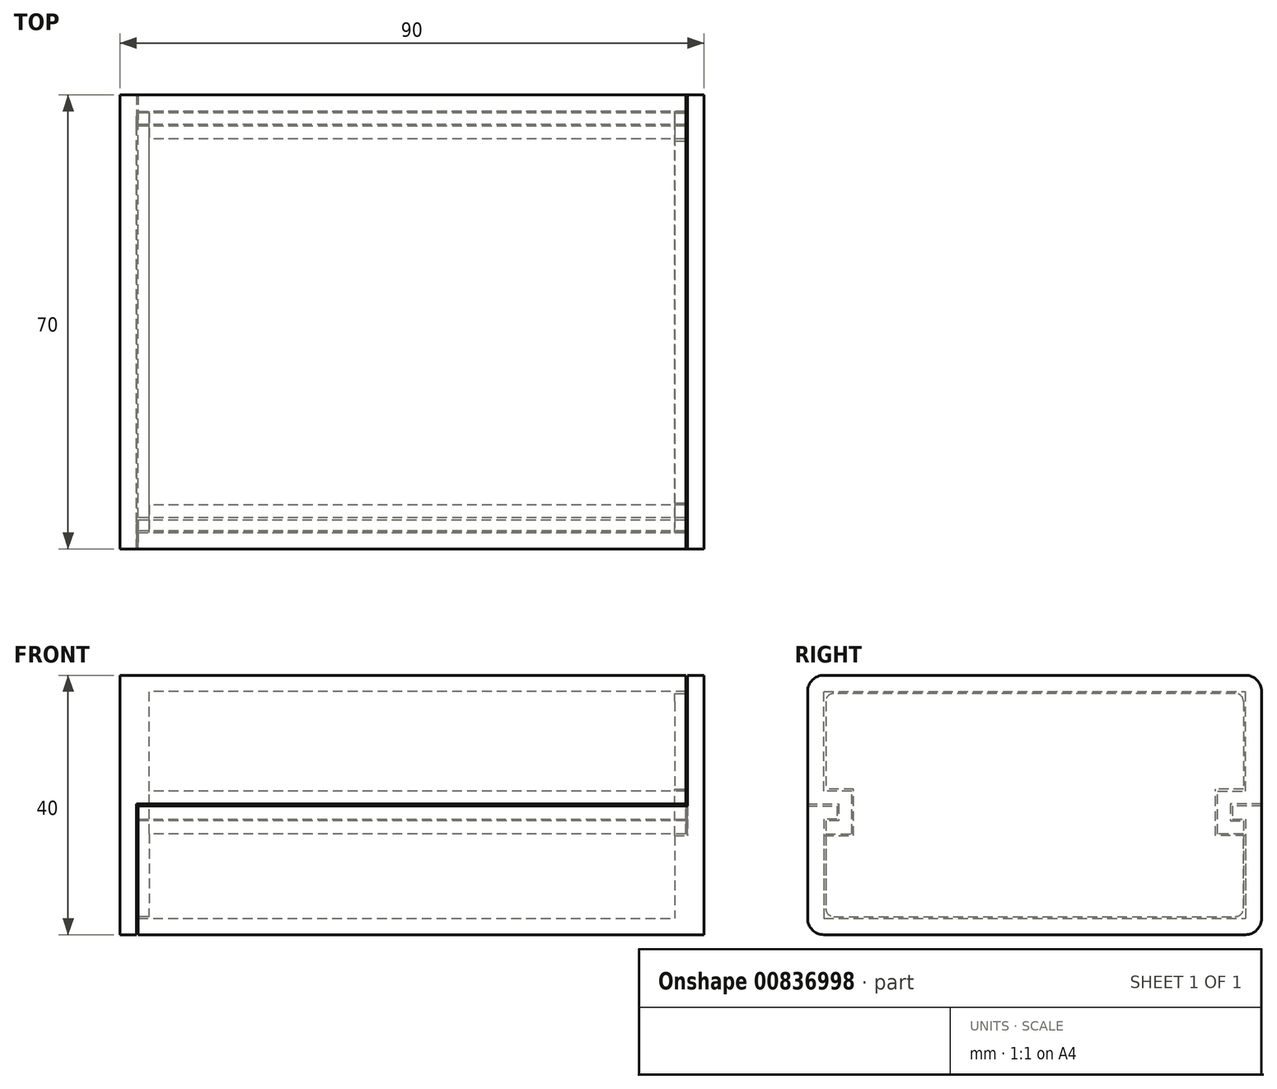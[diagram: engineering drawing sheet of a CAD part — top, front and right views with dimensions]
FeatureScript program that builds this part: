
annotation { "Feature Type Name" : "Feature", "Feature Type Description" : "" }
export const myFeature = defineFeature(function(context is Context, id is Id, definition is map)
    precondition{}
    {
        {
            assignVariable(context, id + "F0", {"name" : "LipSize", "anyValue" : 2});
        }
        {
            assignVariable(context, id + "F1", {"name" : "Thickness", "anyValue" : 2.5});
        }
        {
            var Q0;
            Q0=qCreatedBy(makeId("Top.planeOp"),FACE);
            var sketch = newSketch(context, id + "F2", { "sketchPlane" : qUnion([Q0])});
            skLineSegment(sketch, "E0.bottom", {"start": v(-45, 35) * mm, "end": v(45, 35) * mm});
            skLineSegment(sketch, "E0.top", {"start": v(-45, -35) * mm, "end": v(45, -35) * mm});
            skLineSegment(sketch, "E0.left", {"start": v(-45, 35) * mm, "end": v(-45, -35) * mm});
            skLineSegment(sketch, "E0.right", {"start": v(45, 35) * mm, "end": v(45, -35) * mm});
            skLineSegment(sketch, "E1", {"start": v(-42.5, 35) * mm, "end": v(-42.5, -35) * mm, "construction": true});
            skLineSegment(sketch, "E2", {"start": v(42.5, 35) * mm, "end": v(42.5, -35) * mm, "construction": true});
            skLineSegment(sketch, "E3", {"start": v(42.2, 35) * mm, "end": v(42.2, -35) * mm, "construction": true});
            skLineSegment(sketch, "E4", {"start": v(-42.2, 35) * mm, "end": v(-42.2, -35) * mm, "construction": true});
            skSolve(sketch);
        }
        {
            var Q0;
            Q0=qCreatedBy(makeId("Right.planeOp"),FACE);
            var sketch = newSketch(context, id + "F3", { "sketchPlane" : qUnion([Q0])});
            skLineSegment(sketch, "E5.bottom", {"start": v(-35, 20) * mm, "end": v(35, 20) * mm});
            skLineSegment(sketch, "E5.top", {"start": v(-35, -20) * mm, "end": v(35, -20) * mm});
            skLineSegment(sketch, "E5.left", {"start": v(-35, 20) * mm, "end": v(-35, -20) * mm});
            skLineSegment(sketch, "E5.right", {"start": v(35, 20) * mm, "end": v(35, -20) * mm});
            skLineSegment(sketch, "E6", {"start": v(-35, 0) * mm, "end": v(35, 0) * mm, "construction": true});
            skLineSegment(sketch, "E7", {"start": v(35, 17.5) * mm, "end": v(-35, 17.5) * mm, "construction": true});
            skLineSegment(sketch, "E8", {"start": v(35, 17.2) * mm, "end": v(-35, 17.2) * mm, "construction": true});
            skLineSegment(sketch, "E9", {"start": v(35, -17.5) * mm, "end": v(-35, -17.5) * mm, "construction": true});
            skLineSegment(sketch, "E10", {"start": v(-35, -17.2) * mm, "end": v(35, -17.2) * mm, "construction": true});
            skLineSegment(sketch, "E11", {"start": v(32.5, 17.5) * mm, "end": v(32.5, -17.5) * mm, "construction": true});
            skLineSegment(sketch, "E12", {"start": v(-32.5, 17.5) * mm, "end": v(-32.5, -17.5) * mm, "construction": true});
            skSolve(sketch);
        }
        {
            var Q0;
            Q0=makeQuery(id+"F3.imprint","IMPRINT",FACE,{"disambiguationData":[TD([[makeQuery(id+"F3.imprint","IMPRINT",EDGE,{"derivedFrom":sQuery(id+"F3.wireOp",EDGE,"E5.bottom")}),-1.0]])]});
            var sketch = newSketch(context, id + "F4", { "sketchPlane" : qUnion([Q0])});
            skLineSegment(sketch, "E13", {"start": v(-35, -0.15) * mm, "end": v(-35, -20) * mm});
            skLineSegment(sketch, "E14.0", {"start": v(-35, -20) * mm, "end": v(35, -20) * mm});
            skLineSegment(sketch, "E15.0", {"start": v(-35, 20) * mm, "end": v(35, 20) * mm});
            skLineSegment(sketch, "E16", {"start": v(-35, 20) * mm, "end": v(-35, 0.15) * mm});
            skLineSegment(sketch, "E17", {"start": v(35, 20) * mm, "end": v(35, 0.15) * mm});
            skLineSegment(sketch, "E18", {"start": v(35, -20) * mm, "end": v(35, -0.15) * mm});
            skLineSegment(sketch, "E19", {"start": v(-35, -0.15) * mm, "end": v(-30.5, -0.15) * mm});
            skLineSegment(sketch, "E20", {"start": v(-30.5, -0.15) * mm, "end": v(-30.5, -2.15) * mm});
            skLineSegment(sketch, "E21", {"start": v(-30.5, -2.15) * mm, "end": v(-32.5, -2.15) * mm});
            skLineSegment(sketch, "E22", {"start": v(-32.5, -2.15) * mm, "end": v(-32.5, -17.5) * mm});
            skLineSegment(sketch, "E23", {"start": v(0, 20) * mm, "end": v(0, -20) * mm, "construction": true});
            skLineSegment(sketch, "E24", {"start": v(-32.5, -17.5) * mm, "end": v(32.5, -17.5) * mm});
            skLineSegment(sketch, "E25", {"start": v(-35, 0.15) * mm, "end": v(-30.2, 0.15) * mm});
            skLineSegment(sketch, "E26", {"start": v(-30.2, 0.15) * mm, "end": v(-30.2, -2.45) * mm});
            skLineSegment(sketch, "E27", {"start": v(-30.2, -2.45) * mm, "end": v(-32.2, -2.45) * mm});
            skLineSegment(sketch, "E28", {"start": v(-32.2, -2.45) * mm, "end": v(-32.2, -4.45) * mm});
            skLineSegment(sketch, "E29", {"start": v(-32.2, -4.45) * mm, "end": v(-28.2, -4.45) * mm});
            skLineSegment(sketch, "E30", {"start": v(-28.2, -4.45) * mm, "end": v(-28.2, 2.15) * mm});
            skLineSegment(sketch, "E31", {"start": v(-28.2, 2.15) * mm, "end": v(-32.5, 2.15) * mm});
            skLineSegment(sketch, "E32", {"start": v(-32.5, 2.15) * mm, "end": v(-32.5, 17.5) * mm});
            skLineSegment(sketch, "E33", {"start": v(-32.5, 17.5) * mm, "end": v(32.5, 17.5) * mm});
            skLineSegment(sketch, "E34.MirrorCS", {"start": v(35, -0.15) * mm, "end": v(35, -20) * mm});
            skLineSegment(sketch, "E35.MirrorCS", {"start": v(32.2, -4.45) * mm, "end": v(28.2, -4.45) * mm});
            skLineSegment(sketch, "E36.MirrorCS", {"start": v(32.2, -2.45) * mm, "end": v(32.2, -4.45) * mm});
            skLineSegment(sketch, "E37.MirrorCS", {"start": v(32.5, -2.15) * mm, "end": v(32.5, -17.5) * mm});
            skLineSegment(sketch, "E38.MirrorCS", {"start": v(28.2, 2.15) * mm, "end": v(32.5, 2.15) * mm});
            skLineSegment(sketch, "E39.MirrorCS", {"start": v(30.2, -2.45) * mm, "end": v(32.2, -2.45) * mm});
            skLineSegment(sketch, "E40.MirrorCS", {"start": v(35, -0.15) * mm, "end": v(30.5, -0.15) * mm});
            skLineSegment(sketch, "E41.MirrorCS", {"start": v(30.5, -2.15) * mm, "end": v(32.5, -2.15) * mm});
            skLineSegment(sketch, "E42.MirrorCS", {"start": v(35, 0.15) * mm, "end": v(30.2, 0.15) * mm});
            skLineSegment(sketch, "E43.MirrorCS", {"start": v(30.5, -0.15) * mm, "end": v(30.5, -2.15) * mm});
            skLineSegment(sketch, "E44.MirrorCS", {"start": v(30.2, 0.15) * mm, "end": v(30.2, -2.45) * mm});
            skLineSegment(sketch, "E45.MirrorCS", {"start": v(32.5, 2.15) * mm, "end": v(32.5, 17.5) * mm});
            skLineSegment(sketch, "E46.MirrorCS", {"start": v(28.2, -4.45) * mm, "end": v(28.2, 2.15) * mm});
            skSolve(sketch);
        }
        {
            var Q0;
            Q0=makeQuery(id+"F4.imprint","IMPRINT",FACE,{"disambiguationData":[TD([[makeQuery(id+"F4.imprint","IMPRINT",EDGE,{"derivedFrom":sQuery(id+"F4.wireOp",EDGE,"E15.0")}),-1.0]])]});
            var Q1;
            Q1=sQuery(id+"F2.wireOp",VERTEX,"E3.end");
            var Q2;
            Q2=sQuery(id+"F2.wireOp",VERTEX,"E1.end");
            extrude(context, id + "F5", {"entities" : qUnion([Q0]), "endBound" : BoundingType.UP_TO_VERTEX, "depth" : 25 * mm, "endBoundEntityVertex" : qUnion([Q1]), "offsetDistance" : 25 * mm, "hasSecondDirection" : true, "secondDirectionBound" : SecondDirectionBoundingType.UP_TO_VERTEX, "secondDirectionOppositeDirection" : true, "secondDirectionDepth" : 25 * mm, "secondDirectionBoundEntityVertex" : qUnion([Q2])});
        }
        {
            var Q0;
            Q0=makeQuery(id+"F4.imprint","IMPRINT",FACE,{"disambiguationData":[TD([[makeQuery(id+"F4.imprint","IMPRINT",EDGE,{"derivedFrom":sQuery(id+"F4.wireOp",EDGE,"E13")}),1.0]])]});
            var Q1;
            Q1=sQuery(id+"F2.wireOp",VERTEX,"E4.end");
            var Q2;
            Q2=sQuery(id+"F2.wireOp",VERTEX,"E2.end");
            extrude(context, id + "F6", {"entities" : qUnion([Q0]), "endBound" : BoundingType.UP_TO_VERTEX, "oppositeDirection" : true, "depth" : 25 * mm, "endBoundEntityVertex" : qUnion([Q1]), "offsetDistance" : 25 * mm, "hasSecondDirection" : true, "secondDirectionBound" : SecondDirectionBoundingType.UP_TO_VERTEX, "secondDirectionOppositeDirection" : false, "secondDirectionDepth" : 25 * mm, "secondDirectionBoundEntityVertex" : qUnion([Q2])});
        }
        {
            var Q0;
            Q0=makeQuery(id+"F5.opExtrude","CAP_FACE",FACE,{"disambiguationData":[OSD([sQuery(id+"F4.wireOp",EDGE,"E15.0"),sQuery(id+"F4.wireOp",EDGE,"E16"),sQuery(id+"F4.wireOp",EDGE,"E25"),sQuery(id+"F4.wireOp",EDGE,"E26"),sQuery(id+"F4.wireOp",EDGE,"E27"),sQuery(id+"F4.wireOp",EDGE,"E28"),sQuery(id+"F4.wireOp",EDGE,"E29"),sQuery(id+"F4.wireOp",EDGE,"E30"),sQuery(id+"F4.wireOp",EDGE,"E31"),sQuery(id+"F4.wireOp",EDGE,"E32"),sQuery(id+"F4.wireOp",EDGE,"E33"),sQuery(id+"F4.wireOp",EDGE,"E17"),sQuery(id+"F4.wireOp",EDGE,"E35.MirrorCS"),sQuery(id+"F4.wireOp",EDGE,"E36.MirrorCS"),sQuery(id+"F4.wireOp",EDGE,"E38.MirrorCS"),sQuery(id+"F4.wireOp",EDGE,"E39.MirrorCS"),sQuery(id+"F4.wireOp",EDGE,"E42.MirrorCS"),sQuery(id+"F4.wireOp",EDGE,"E44.MirrorCS"),sQuery(id+"F4.wireOp",EDGE,"E45.MirrorCS"),sQuery(id+"F4.wireOp",EDGE,"E46.MirrorCS")])],"isStart":true});
            var sketch = newSketch(context, id + "F7", { "sketchPlane" : qUnion([Q0])});
            skLineSegment(sketch, "E47.bottom", {"start": v(-35, 20) * mm, "end": v(35, 20) * mm});
            skLineSegment(sketch, "E47.top", {"start": v(-35, -20) * mm, "end": v(35, -20) * mm});
            skLineSegment(sketch, "E47.left", {"start": v(-35, 20) * mm, "end": v(-35, -20) * mm});
            skLineSegment(sketch, "E47.right", {"start": v(35, 20) * mm, "end": v(35, -20) * mm});
            skSolve(sketch);
        }
        {
            var Q0;
            Q0=qSketchRegion(id+"F7",true);
            var Q1;
            Q1=sQuery(id+"F2.wireOp",VERTEX,"E0.bottom.start");
            extrude(context, id + "F8", {"entities" : qUnion([Q0]), "operationType" : NewBodyOperationType.ADD, "endBound" : BoundingType.UP_TO_VERTEX, "depth" : 25 * mm, "endBoundEntityVertex" : qUnion([Q1]), "offsetDistance" : 25 * mm});
        }
        {
            var Q0;
            Q0=makeQuery(id+"F6.opExtrude","CAP_FACE",FACE,{"disambiguationData":[OSD([sQuery(id+"F4.wireOp",EDGE,"E13"),sQuery(id+"F4.wireOp",EDGE,"E14.0"),sQuery(id+"F4.wireOp",EDGE,"E19"),sQuery(id+"F4.wireOp",EDGE,"E20"),sQuery(id+"F4.wireOp",EDGE,"E21"),sQuery(id+"F4.wireOp",EDGE,"E22"),sQuery(id+"F4.wireOp",EDGE,"E24"),sQuery(id+"F4.wireOp",EDGE,"E34.MirrorCS"),sQuery(id+"F4.wireOp",EDGE,"E37.MirrorCS"),sQuery(id+"F4.wireOp",EDGE,"E40.MirrorCS"),sQuery(id+"F4.wireOp",EDGE,"E41.MirrorCS"),sQuery(id+"F4.wireOp",EDGE,"E43.MirrorCS")])],"isStart":true});
            var sketch = newSketch(context, id + "F9", { "sketchPlane" : qUnion([Q0])});
            skLineSegment(sketch, "E48.bottom", {"start": v(35, -20) * mm, "end": v(-35, -20) * mm});
            skLineSegment(sketch, "E48.top", {"start": v(35, 20) * mm, "end": v(-35, 20) * mm});
            skLineSegment(sketch, "E48.left", {"start": v(35, -20) * mm, "end": v(35, 20) * mm});
            skLineSegment(sketch, "E48.right", {"start": v(-35, -20) * mm, "end": v(-35, 20) * mm});
            skSolve(sketch);
        }
        {
            var Q0;
            Q0=qSketchRegion(id+"F9",true);
            var Q1;
            Q1=sQuery(id+"F2.wireOp",VERTEX,"E0.top.end");
            extrude(context, id + "F10", {"entities" : qUnion([Q0]), "operationType" : NewBodyOperationType.ADD, "endBound" : BoundingType.UP_TO_VERTEX, "depth" : 25 * mm, "endBoundEntityVertex" : qUnion([Q1]), "offsetDistance" : 25 * mm});
        }
        {
            var Q0;
            Q0=makeQuery(id+"F8.opExtrude","CAP_FACE",FACE,{"disambiguationData":[OSD([sQuery(id+"F7.wireOp",EDGE,"E47.bottom"),sQuery(id+"F7.wireOp",EDGE,"E47.top"),sQuery(id+"F7.wireOp",EDGE,"E47.left"),sQuery(id+"F7.wireOp",EDGE,"E47.right")])],"isStart":true});
            var sketch = newSketch(context, id + "F11", { "sketchPlane" : qUnion([Q0])});
            skLineSegment(sketch, "E49", {"start": v(-32.2, -4.45) * mm, "end": v(-32.2, -17.2) * mm});
            skLineSegment(sketch, "E50", {"start": v(-32.2, -17.2) * mm, "end": v(32.2, -17.2) * mm});
            skLineSegment(sketch, "E51", {"start": v(32.2, -17.2) * mm, "end": v(32.2, -4.45) * mm});
            skSolve(sketch);
        }
        {
            var Q0;
            Q0=makeQuery(id+"F11.imprint","IMPRINT",FACE,{"disambiguationData":[TD([[makeQuery(id+"F11.imprint","IMPRINT",EDGE,{"derivedFrom":sQuery(id+"F11.wireOp",EDGE,"E49")}),1.0]])]});
            extrude(context, id + "F12", {"entities" : qUnion([Q0]), "operationType" : NewBodyOperationType.ADD, "depth" : (getVariable(context, 'LipSize')) * mm, "offsetDistance" : 25 * mm});
        }
        {
            var Q0;
            Q0=makeQuery(id+"F10.opExtrude","CAP_FACE",FACE,{"disambiguationData":[OSD([sQuery(id+"F9.wireOp",EDGE,"E48.bottom"),sQuery(id+"F9.wireOp",EDGE,"E48.top"),sQuery(id+"F9.wireOp",EDGE,"E48.left"),sQuery(id+"F9.wireOp",EDGE,"E48.right")])],"isStart":true});
            var sketch = newSketch(context, id + "F13", { "sketchPlane" : qUnion([Q0])});
            skLineSegment(sketch, "E52.bottom", {"start": v(-32.2, 17.2) * mm, "end": v(32.2, 17.2) * mm});
            skLineSegment(sketch, "E52.top", {"start": v(-32.2, 2.45) * mm, "end": v(-27.9, 2.45) * mm});
            skLineSegment(sketch, "E52.left", {"start": v(-32.2, 17.2) * mm, "end": v(-32.2, 2.45) * mm});
            skLineSegment(sketch, "E52.right", {"start": v(32.2, 17.2) * mm, "end": v(32.2, 2.45) * mm});
            skLineSegment(sketch, "E53", {"start": v(-32.5, -4.75) * mm, "end": v(-27.9, -4.75) * mm});
            skLineSegment(sketch, "E54", {"start": v(-27.9, -4.75) * mm, "end": v(-27.9, 2.45) * mm});
            skLineSegment(sketch, "E55.MirrorCS", {"start": v(27.9, -4.75) * mm, "end": v(27.9, 2.45) * mm});
            skLineSegment(sketch, "E56.MirrorCS", {"start": v(32.5, -4.75) * mm, "end": v(27.9, -4.75) * mm});
            skLineSegment(sketch, "E57.trimOffspring", {"start": v(27.9, 2.45) * mm, "end": v(32.2, 2.45) * mm});
            skSolve(sketch);
        }
        {
            var Q0;
            Q0=makeQuery(id+"F13.imprint","IMPRINT",FACE,{"disambiguationData":[TD([[makeQuery(id+"F13.imprint","IMPRINT",EDGE,{"derivedFrom":sQuery(id+"F13.wireOp",EDGE,"E52.bottom")}),-1.0]])]});
            extrude(context, id + "F14", {"entities" : qUnion([Q0]), "operationType" : NewBodyOperationType.ADD, "depth" : (getVariable(context, 'LipSize')) * mm, "offsetDistance" : 25 * mm});
        }
        {
            var Q0;
            Q0=makeQuery(id+"F8.boolean.opBoolean","MERGE",EDGE,{"derivedFrom":[makeQuery(id+"F5.opExtrude","TWEAK_EDGE",EDGE,{"derivedFrom":[makeQuery(id+"F4.imprint","IMPRINT",EDGE,{"derivedFrom":sQuery(id+"F4.wireOp",EDGE,"E15.0")}),makeQuery(id+"F4.imprint","IMPRINT",EDGE,{"derivedFrom":sQuery(id+"F4.wireOp",EDGE,"E16")})]}),makeQuery(id+"F8.opExtrude","SWEPT_EDGE",EDGE,{"disambiguationData":[OSD([sQuery(id+"F7.wireOp",EDGE,"E47.bottom"),sQuery(id+"F7.wireOp",EDGE,"E47.right")])]})]});
            var Q1;
            Q1=makeQuery(id+"F8.boolean.opBoolean","MERGE",EDGE,{"derivedFrom":[makeQuery(id+"F5.opExtrude","TWEAK_EDGE",EDGE,{"derivedFrom":[makeQuery(id+"F4.imprint","IMPRINT",EDGE,{"derivedFrom":sQuery(id+"F4.wireOp",EDGE,"E15.0")}),makeQuery(id+"F4.imprint","IMPRINT",EDGE,{"derivedFrom":sQuery(id+"F4.wireOp",EDGE,"E17")})]}),makeQuery(id+"F8.opExtrude","SWEPT_EDGE",EDGE,{"disambiguationData":[OSD([sQuery(id+"F7.wireOp",EDGE,"E47.bottom"),sQuery(id+"F7.wireOp",EDGE,"E47.left")])]})]});
            var Q2;
            Q2=makeQuery(id+"F10.boolean.opBoolean","MERGE",EDGE,{"derivedFrom":[makeQuery(id+"F6.opExtrude","TWEAK_EDGE",EDGE,{"derivedFrom":[makeQuery(id+"F4.imprint","IMPRINT",EDGE,{"derivedFrom":sQuery(id+"F4.wireOp",EDGE,"E13")}),makeQuery(id+"F4.imprint","IMPRINT",EDGE,{"derivedFrom":sQuery(id+"F4.wireOp",EDGE,"E14.0")})]}),makeQuery(id+"F10.opExtrude","SWEPT_EDGE",EDGE,{"disambiguationData":[OSD([sQuery(id+"F9.wireOp",EDGE,"E48.bottom"),sQuery(id+"F9.wireOp",EDGE,"E48.right")])]})]});
            var Q3;
            Q3=makeQuery(id+"F8.opExtrude","SWEPT_EDGE",EDGE,{"disambiguationData":[OSD([sQuery(id+"F7.wireOp",EDGE,"E47.top"),sQuery(id+"F7.wireOp",EDGE,"E47.right")])]});
            var Q4;
            Q4=makeQuery(id+"F10.opExtrude","SWEPT_EDGE",EDGE,{"disambiguationData":[OSD([sQuery(id+"F9.wireOp",EDGE,"E48.top"),sQuery(id+"F9.wireOp",EDGE,"E48.right")])]});
            var Q5;
            Q5=makeQuery(id+"F10.opExtrude","SWEPT_EDGE",EDGE,{"disambiguationData":[OSD([sQuery(id+"F9.wireOp",EDGE,"E48.top"),sQuery(id+"F9.wireOp",EDGE,"E48.left")])]});
            var Q6;
            Q6=makeQuery(id+"F8.opExtrude","SWEPT_EDGE",EDGE,{"disambiguationData":[OSD([sQuery(id+"F7.wireOp",EDGE,"E47.top"),sQuery(id+"F7.wireOp",EDGE,"E47.left")])]});
            var Q7;
            Q7=makeQuery(id+"F10.boolean.opBoolean","MERGE",EDGE,{"derivedFrom":[makeQuery(id+"F6.opExtrude","TWEAK_EDGE",EDGE,{"derivedFrom":[makeQuery(id+"F4.imprint","IMPRINT",EDGE,{"derivedFrom":sQuery(id+"F4.wireOp",EDGE,"E14.0")}),makeQuery(id+"F4.imprint","IMPRINT",EDGE,{"derivedFrom":sQuery(id+"F4.wireOp",EDGE,"E34.MirrorCS")})]}),makeQuery(id+"F10.opExtrude","SWEPT_EDGE",EDGE,{"disambiguationData":[OSD([sQuery(id+"F9.wireOp",EDGE,"E48.bottom"),sQuery(id+"F9.wireOp",EDGE,"E48.left")])]})]});
            fillet(context, id + "F15", {"entities" : qUnion([Q0, Q1, Q2, Q3, Q4, Q5, Q6, Q7]), "radius" : (getVariable(context, 'Thickness')) * mm, "tangentPropagation" : true, "allowEdgeOverflow" : false});
        }
        {
            var Q0;
            Q0=makeQuery(id+"F12.opExtrude","SWEPT_EDGE",EDGE,{"disambiguationData":[OSD([sQuery(id+"F11.wireOp",EDGE,"E49"),sQuery(id+"F11.wireOp",EDGE,"E50")])]});
            var Q1;
            Q1=makeQuery(id+"F12.opExtrude","SWEPT_EDGE",EDGE,{"disambiguationData":[OSD([sQuery(id+"F11.wireOp",EDGE,"E50"),sQuery(id+"F11.wireOp",EDGE,"E51")])]});
            var Q2;
            Q2=makeQuery(id+"F5.opExtrude","TWEAK_EDGE",EDGE,{"derivedFrom":[makeQuery(id+"F4.imprint","IMPRINT",EDGE,{"derivedFrom":sQuery(id+"F4.wireOp",EDGE,"E32")}),makeQuery(id+"F4.imprint","IMPRINT",EDGE,{"derivedFrom":sQuery(id+"F4.wireOp",EDGE,"E33")})]});
            var Q3;
            Q3=makeQuery(id+"F5.opExtrude","TWEAK_EDGE",EDGE,{"derivedFrom":[makeQuery(id+"F4.imprint","IMPRINT",EDGE,{"derivedFrom":sQuery(id+"F4.wireOp",EDGE,"E33")}),makeQuery(id+"F4.imprint","IMPRINT",EDGE,{"derivedFrom":sQuery(id+"F4.wireOp",EDGE,"E45.MirrorCS")})]});
            var Q4;
            Q4=makeQuery(id+"F6.opExtrude","TWEAK_EDGE",EDGE,{"derivedFrom":[makeQuery(id+"F4.imprint","IMPRINT",EDGE,{"derivedFrom":sQuery(id+"F4.wireOp",EDGE,"E22")}),makeQuery(id+"F4.imprint","IMPRINT",EDGE,{"derivedFrom":sQuery(id+"F4.wireOp",EDGE,"E24")})]});
            var Q5;
            Q5=makeQuery(id+"F6.opExtrude","TWEAK_EDGE",EDGE,{"derivedFrom":[makeQuery(id+"F4.imprint","IMPRINT",EDGE,{"derivedFrom":sQuery(id+"F4.wireOp",EDGE,"E24")}),makeQuery(id+"F4.imprint","IMPRINT",EDGE,{"derivedFrom":sQuery(id+"F4.wireOp",EDGE,"E37.MirrorCS")})]});
            var Q6;
            Q6=makeQuery(id+"F14.opExtrude","SWEPT_EDGE",EDGE,{"disambiguationData":[OSD([sQuery(id+"F13.wireOp",EDGE,"E52.bottom"),sQuery(id+"F13.wireOp",EDGE,"E52.left")])]});
            var Q7;
            Q7=makeQuery(id+"F14.opExtrude","SWEPT_EDGE",EDGE,{"disambiguationData":[OSD([sQuery(id+"F13.wireOp",EDGE,"E52.bottom"),sQuery(id+"F13.wireOp",EDGE,"E52.right")])]});
            fillet(context, id + "F16", {"entities" : qUnion([Q0, Q1, Q2, Q3, Q4, Q5, Q6, Q7]), "radius" : (getVariable(context, 'Thickness') / 2) * mm, "tangentPropagation" : true, "allowEdgeOverflow" : false});
        }
    });
